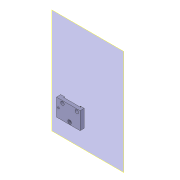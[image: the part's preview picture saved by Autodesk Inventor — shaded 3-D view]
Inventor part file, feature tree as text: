
AUTODESK INVENTOR PART (.ipt)
format: ipt  version: 2019.4 (Build 234330000, 330)  size: 221,696 bytes
history: native  units: mm
features: extrude x6, sketch x6, reference x6, projected_geometry x4, other x4, plane x1
ambient origin geometry x8: Origin, YZ Plane, XZ Plane, XY Plane, X Axis, Y Axis, Z Axis, Center Point
bodies: Solid1 (feature_tree)
feature tree (27):
  plane  "Work Plane1"
  extrude  "Extrusion1"  Depth=4.0mm
  extrude  "Extrusion2"  Depth=4.0mm
  extrude  "Extrusion3"  Depth=5.9mm
  extrude  "Extrusion4"  Depth=10.0mm
  extrude  "Extrusion5"  Depth=1.5mm
  extrude  "Extrusion6"  Depth=2.0mm
  sketch  "Sketch1"  dims[d0=4.0mm d2=4.0mm]
  reference  "Reference1"
  reference  "Reference2"
  reference  "Reference3"
  reference  "Reference4"
  reference  "Reference5"
  sketch  "Sketch2"  dims[d3=4.0mm d4=5.9mm]
  projected_geometry  "Projected Loop1"
  sketch  "Sketch3"  dims[d5=5.9mm d6=5.9mm]
  projected_geometry  "Projected Loop2"
  reference  "Reference6"
  sketch  "Sketch4"  dims[d7=4.0mm d8=0.0mm d10=10.0mm]
  projected_geometry  "Projected Loop3"
  sketch  "Sketch5"  dims[d11=1.5mm d12=0.0mm d13=27.0mm]
  sketch  "Sketch6"  dims[d14=1.0mm d15=6.0mm d16=1.2mm d19=0.2mm d22=0.5mm d23=0.0mm d28=2.0mm d29=0.0mm d30=2.8mm d31=2.8mm d32=0.0mm d33=0.5mm d34=0.0mm d35=24.248711mm d36=12.124356mm]
  projected_geometry  "Projected Loop4"
  other  "cellSTORM_v5.iam"
  other  "cellSTORM_Base_v0_R1:1"
  other  "cellSTORM_nickelplate:1"
  other  "00_chip_01_old:1"
